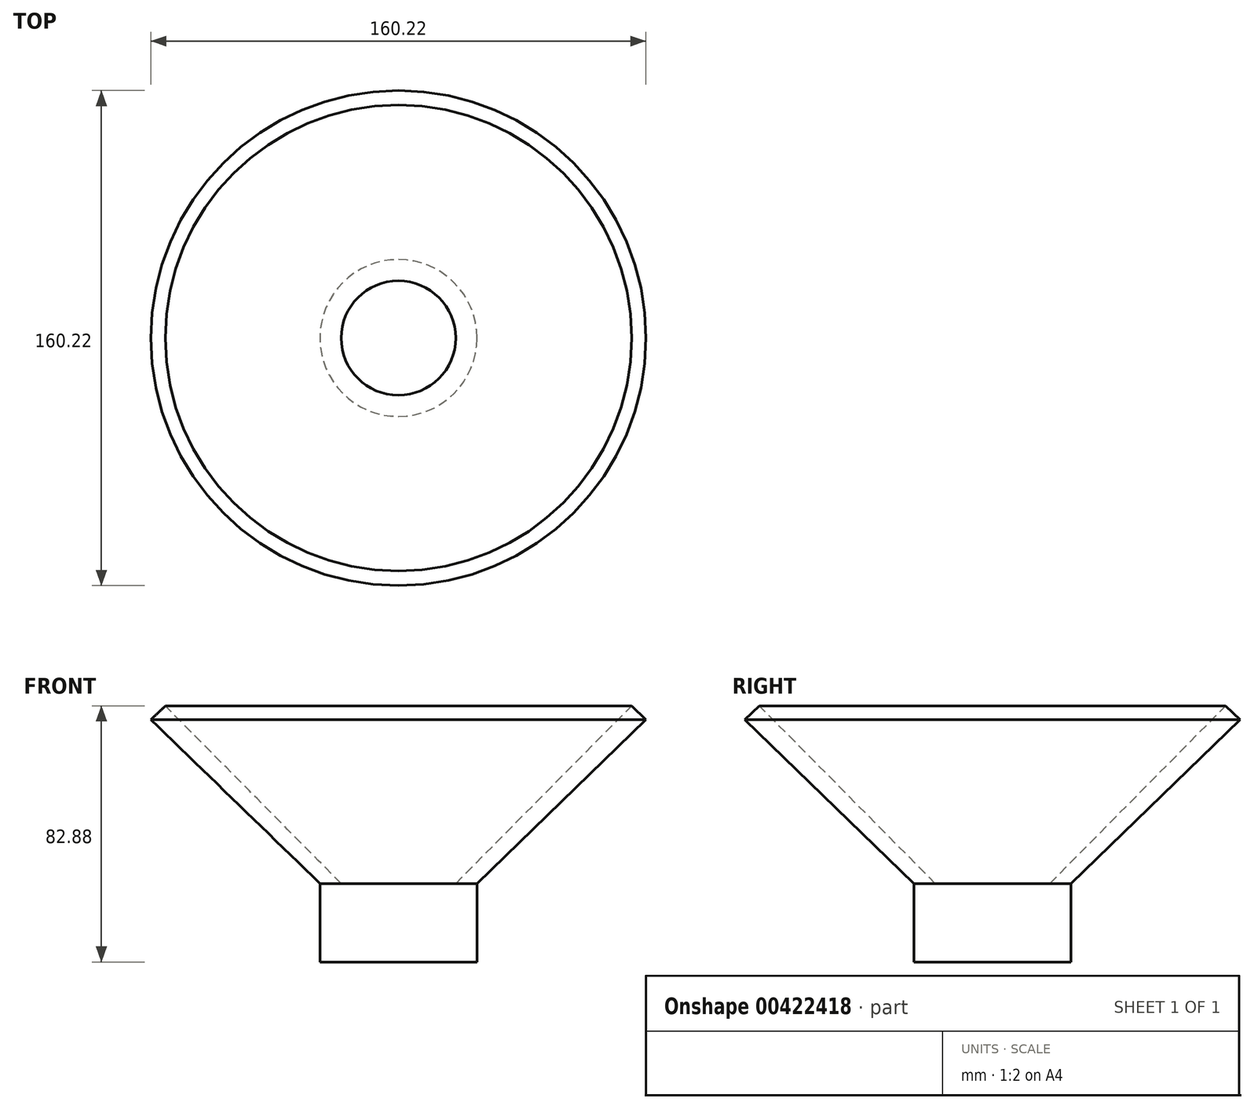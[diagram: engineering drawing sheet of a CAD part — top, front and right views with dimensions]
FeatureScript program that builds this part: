
annotation { "Feature Type Name" : "Feature", "Feature Type Description" : "" }
export const myFeature = defineFeature(function(context is Context, id is Id, definition is map)
    precondition{}
    {
        {
            var Q0;
            Q0=qCreatedBy(makeId("Front.planeOp"),FACE);
            var sketch = newSketch(context, id + "F0", { "sketchPlane" : qUnion([Q0])});
            skLineSegment(sketch, "E0", {"start": v(0, 0) * mm, "end": v(0, -25.4) * mm});
            skLineSegment(sketch, "E1", {"start": v(0, 0) * mm, "end": v(54.7, 53.04) * mm});
            skLineSegment(sketch, "E2", {"start": v(0, -25.4) * mm, "end": v(-25.4, -25.4) * mm});
            skLineSegment(sketch, "E3", {"start": v(-25.4, -25.4) * mm, "end": v(-25.4, 0) * mm});
            skLineSegment(sketch, "E4", {"start": v(-25.4, 0) * mm, "end": v(-6.87, 0) * mm});
            skLineSegment(sketch, "E5", {"start": v(-6.87, 0) * mm, "end": v(50.03, 57.48) * mm});
            skLineSegment(sketch, "E6", {"start": v(50.03, 57.48) * mm, "end": v(54.7, 53.04) * mm});
            skSolve(sketch);
        }
        {
            var Q0;
            Q0 = qSketchRegion(id + "F0", true);
            var Q1;
            Q1=sQuery(id+"F0.wireOp",EDGE,"E3");
            revolve(context, id + "F1", {"entities" : qUnion([Q0]), "axis" : qUnion([Q1]), "revolveType" : RevolveType.FULL});
        }
        {
            var Q0;
            Q0=makeQuery(id+"F1.opRevolve","SWEPT_FACE",FACE,{"disambiguationData":[OSD([sQuery(id+"F0.wireOp",EDGE,"E2")])]});
            var sketch = newSketch(context, id + "F2", { "sketchPlane" : qUnion([Q0])});
            skCircle(sketch, "E7", {"center": v(-25.4, 0) * mm, "radius": 22.9 * mm});
            skSolve(sketch);
        }
        {
            var Q0;
            Q0=makeQuery(id+"F2.imprint","IMPRINT",FACE,{"disambiguationData":[TD([[makeQuery(id+"F2.imprint","IMPRINT",EDGE,{"derivedFrom":sQuery(id+"F2.wireOp",EDGE,"E7")}),1.0]])]});
            extrude(context, id + "F3", {"entities" : qUnion([Q0]), "operationType" : NewBodyOperationType.REMOVE, "depth" : 101.6 * mm});
        }
    });
